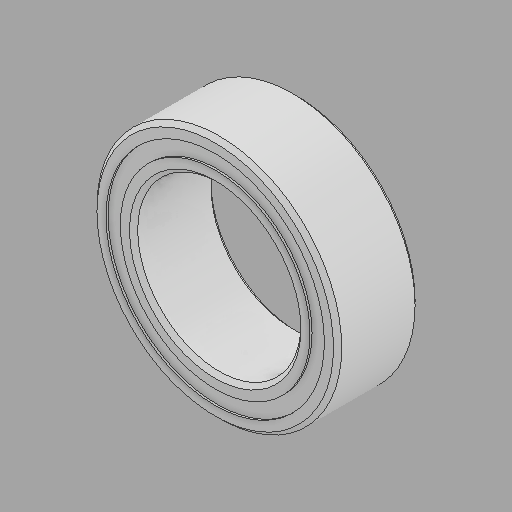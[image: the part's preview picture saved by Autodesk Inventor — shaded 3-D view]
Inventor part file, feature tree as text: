
AUTODESK INVENTOR PART (.ipt)
format: ipt  version: 2024.2 (Build 282272000, 272)  size: 587,776 bytes
history: native  units: in
note: dims shown in document units (in); Inventor stores cm internally (conversion verified against a paired STEP export)
features: other x11, revolve x5
ambient origin geometry x8: Origin, YZ Plane, XZ Plane, XY Plane, X Axis, Y Axis, Z Axis, Center Point
bodies: Solid1 (feature_tree), Solid2 (feature_tree), Solid3 (feature_tree), Solid4 (feature_tree), Solid5 (feature_tree), Solid6 (feature_tree), Solid7 (feature_tree), Solid8 (feature_tree), Solid9 (feature_tree), Solid10 (feature_tree), Solid11 (feature_tree), Solid12 (feature_tree), Solid13 (feature_tree), Solid14 (feature_tree), Solid15 (feature_tree), Solid16 (feature_tree)
feature tree (16):
  revolve  "Revolve1"  [1 undecoded]
  revolve  "Revolve3"  [1 undecoded]
  revolve  "Revolve4"  [1 undecoded]
  other  "CirPattern1[1]"
  other  "CirPattern1[2]"
  other  "CirPattern1[3]"
  other  "CirPattern1[4]"
  other  "CirPattern1[5]"
  other  "CirPattern1[6]"
  other  "CirPattern1[7]"
  other  "CirPattern1[8]"
  other  "CirPattern1[9]"
  other  "CirPattern1[10]"
  other  "CirPattern1[11]"
  revolve  "Revolve5[1]"  [1 undecoded]
  revolve  "Revolve5[2]"  [1 undecoded]
note: 5 required parameter values undecoded (feature->parameter linkage not recoverable at this tier; creation-order binding heuristic only, values carry confidence <= 0.55)
